# Revit family: Casement Arch Top w Mullions-Number
name_source: partatom
category: Windows
revit_build: Autodesk Revit Architecture 2012 (Build: 20110309_2315(x64)
units: mm (PartAtom-declared; Revit-internal decimal feet)

## types (10) — shared parameters
Assembly Code = B2020100
Glass Pane Material = Glass
Sash Material = Sash
Sill HT = 1' - 0"
Trim Exterior Material = Trim
Trim Interior Material = Trim
Trim Projection - Ext. = 0' - 0 1/2"
Trim Projection - Int. = 0' - 0 3/4"
Trim Width - Exterior = 0' - 3 1/2"
Trim Width - Interior = 0' - 3 1/2"
Wall Closure = By host

## per-type parameters (varying)
| type | Header Height | Height | Horizontal Lites | MHeight | MWidth | Spring Ht | Vertical Lites | Width | Window Inset |
| 36" x 48" | 6' - 2" | 4' - 0" | 4 | 4' - 3" | 2' - 7" | 0' - 8" | 4 | 3' - 0" | 0' - 0 3/4" |
| 36" x 60" | 2' - 10" | 0' - 8" | 3 | 0' - 11" | 2' - 7" | 0' - 8" | 5 | 3' - 0" | 0' - 5 1/2" |
| 36" x 72" | 2' - 9 3/4" | 0' - 7 7/8" | 3 | 0' - 10 3/4" | 2' - 7" | 0' - 7 7/8" | 6 | 3' - 0" | 0' - 0 3/4" |
| 12" x 48" | 2' - 9 3/4" | 0' - 7 7/8" | 1 | 0' - 10 3/4" | 0' - 7" | 0' - 7 7/8" | 4 | 1' - 0" | 0' - 0 3/4" |
| 12" x 12" | 2' - 9 3/4" | 0' - 7 7/8" | 0 | 0' - 10 3/4" | 0' - 7" | 0' - 7 7/8" | 0 | 1' - 0" | 0' - 0 3/4" |
| 24" x 24" | 2' - 9 3/4" | 0' - 7 7/8" | 2 | 0' - 10 3/4" | 1' - 7" | 0' - 7 7/8" | 2 | 2' - 0" | 0' - 0 3/4" |
| 48" x 48" | 2' - 9 3/4" | 0' - 7 7/8" | 5 | 0' - 10 3/4" | 3' - 7" | 0' - 7 7/8" | 5 | 4' - 0" | 0' - 0 3/4" |
| 24" x 48" | 2' - 9 3/4" | 0' - 7 7/8" | 2 | 0' - 10 3/4" | 1' - 7" | 0' - 7 7/8" | 4 | 2' - 0" | 0' - 0 3/4" |
| 36" x 36" | 2' - 9 3/4" | 0' - 7 7/8" | 3 | 0' - 10 3/4" | 2' - 7" | 0' - 7 7/8" | 3 | 3' - 0" | 0' - 0 3/4" |
| 3670 | 2' - 10" | 0' - 8" | 3 | 0' - 11" | 3' - 1" | 0' - 8" | 4 | 3' - 6" | 0' - 3 3/4" |

## geometry (parser evidence)
native form markers: Blend x2, Sweep x19
no freeform markers — native parametric forms only
